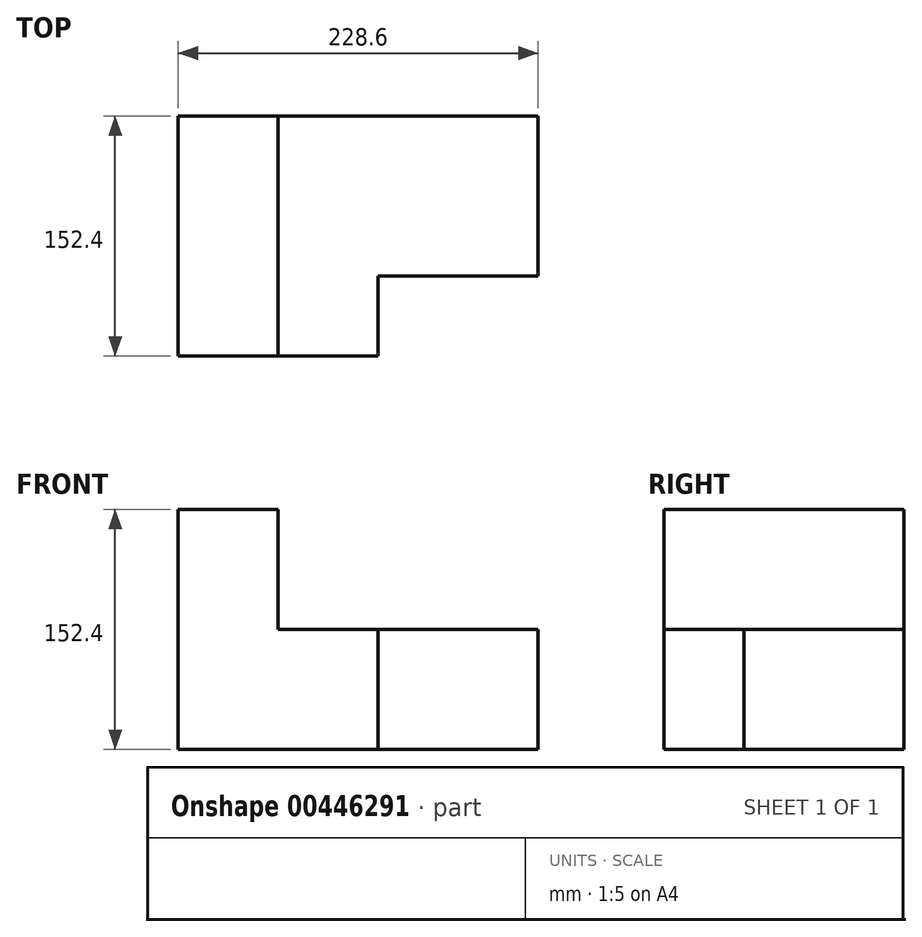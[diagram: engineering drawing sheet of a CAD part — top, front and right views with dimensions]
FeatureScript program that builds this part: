
annotation { "Feature Type Name" : "Feature", "Feature Type Description" : "" }
export const myFeature = defineFeature(function(context is Context, id is Id, definition is map)
    precondition{}
    {
        {
            var Q0;
            Q0=qCreatedBy(makeId("Front.planeOp"),FACE);
            var sketch = newSketch(context, id + "F0", { "sketchPlane" : qUnion([Q0])});
            skLineSegment(sketch, "E0.bottom", {"start": v(-109.3, 82.24) * mm, "end": v(119.3, 82.24) * mm});
            skLineSegment(sketch, "E0.top", {"start": v(-109.3, -70.16) * mm, "end": v(119.3, -70.16) * mm});
            skLineSegment(sketch, "E0.left", {"start": v(-109.3, 82.24) * mm, "end": v(-109.3, -70.16) * mm});
            skLineSegment(sketch, "E0.right", {"start": v(119.3, 82.24) * mm, "end": v(119.3, -70.16) * mm});
            skSolve(sketch);
        }
        {
            var Q0;
            Q0=makeQuery(id+"F0.imprint","IMPRINT",FACE,{"disambiguationData":[TD([[makeQuery(id+"F0.imprint","IMPRINT",EDGE,{"derivedFrom":sQuery(id+"F0.wireOp",EDGE,"E0.bottom")}),-1.0]])]});
            extrude(context, id + "F1", {"entities" : qUnion([Q0]), "endBound" : BoundingType.SYMMETRIC, "depth" : 152.4 * mm});
        }
        {
            var Q0;
            Q0=makeQuery(id+"F1.opExtrude","CAP_FACE",FACE,{"disambiguationData":[OSD([sQuery(id+"F0.wireOp",EDGE,"E0.bottom"),sQuery(id+"F0.wireOp",EDGE,"E0.top"),sQuery(id+"F0.wireOp",EDGE,"E0.left"),sQuery(id+"F0.wireOp",EDGE,"E0.right")])],"isStart":false});
            var sketch = newSketch(context, id + "F2", { "sketchPlane" : qUnion([Q0])});
            skLineSegment(sketch, "E1.bottom", {"start": v(119.3, 82.24) * mm, "end": v(-45.8, 82.24) * mm});
            skLineSegment(sketch, "E1.top", {"start": v(119.3, 6.04) * mm, "end": v(-45.8, 6.04) * mm});
            skLineSegment(sketch, "E1.left", {"start": v(119.3, 82.24) * mm, "end": v(119.3, 6.04) * mm});
            skLineSegment(sketch, "E1.right", {"start": v(-45.8, 82.24) * mm, "end": v(-45.8, 6.04) * mm});
            skSolve(sketch);
        }
        {
            var Q0;
            Q0=makeQuery(id+"F2.imprint","IMPRINT",FACE,{"disambiguationData":[TD([[makeQuery(id+"F2.imprint","IMPRINT",EDGE,{"derivedFrom":sQuery(id+"F2.wireOp",EDGE,"E1.bottom")}),-1.0]])]});
            extrude(context, id + "F3", {"entities" : qUnion([Q0]), "operationType" : NewBodyOperationType.REMOVE, "endBound" : BoundingType.THROUGH_ALL, "oppositeDirection" : true, "depth" : 25.4 * mm});
        }
        {
            var Q0;
            Q0=makeQuery(id+"F3.boolean.opBoolean","COPY",FACE,{"derivedFrom":makeQuery(id+"F3.opExtrude","SWEPT_FACE",FACE,{"disambiguationData":[OSD([sQuery(id+"F2.wireOp",EDGE,"E1.top")])]})});
            var sketch = newSketch(context, id + "F4", { "sketchPlane" : qUnion([Q0])});
            skLineSegment(sketch, "E2.bottom", {"start": v(119.3, -76.2) * mm, "end": v(17.7, -76.2) * mm});
            skLineSegment(sketch, "E2.top", {"start": v(119.3, -25.4) * mm, "end": v(17.7, -25.4) * mm});
            skLineSegment(sketch, "E2.left", {"start": v(119.3, -76.2) * mm, "end": v(119.3, -25.4) * mm});
            skLineSegment(sketch, "E2.right", {"start": v(17.7, -76.2) * mm, "end": v(17.7, -25.4) * mm});
            skSolve(sketch);
        }
        {
            var Q0;
            Q0=makeQuery(id+"F4.imprint","IMPRINT",FACE,{"disambiguationData":[TD([[makeQuery(id+"F4.imprint","IMPRINT",EDGE,{"derivedFrom":sQuery(id+"F4.wireOp",EDGE,"E2.bottom")}),-1.0]])]});
            extrude(context, id + "F5", {"entities" : qUnion([Q0]), "operationType" : NewBodyOperationType.REMOVE, "endBound" : BoundingType.THROUGH_ALL, "oppositeDirection" : true, "depth" : 25.4 * mm});
        }
    });
